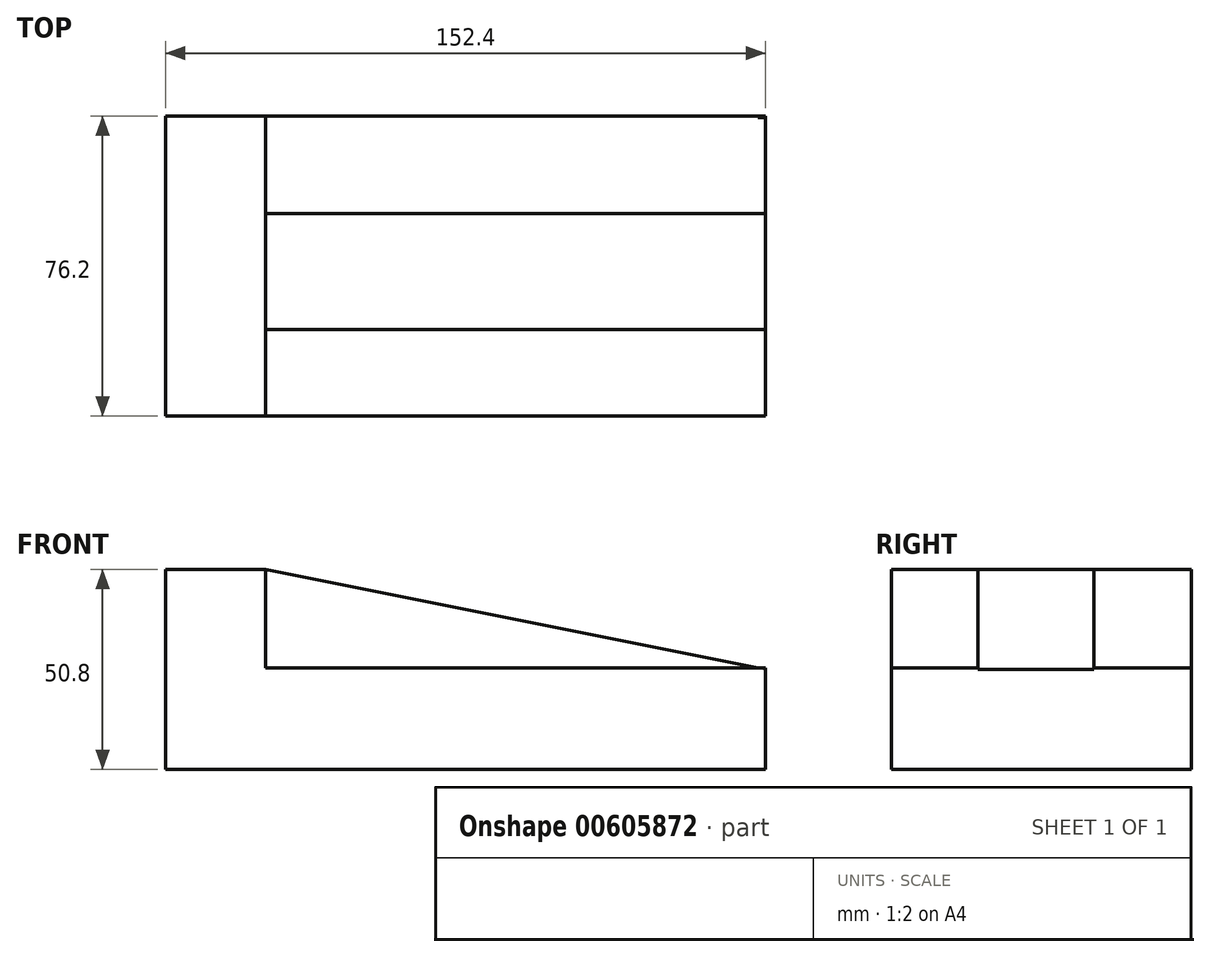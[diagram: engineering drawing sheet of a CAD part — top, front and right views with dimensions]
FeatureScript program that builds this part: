
annotation { "Feature Type Name" : "Feature", "Feature Type Description" : "" }
export const myFeature = defineFeature(function(context is Context, id is Id, definition is map)
    precondition{}
    {
        {
            var Q0;
            Q0=qCreatedBy(makeId("Front.planeOp"),FACE);
            var sketch = newSketch(context, id + "F0", { "sketchPlane" : qUnion([Q0])});
            skLineSegment(sketch, "E0", {"start": v(0, 0) * mm, "end": v(-152.4, 0) * mm});
            skLineSegment(sketch, "E1", {"start": v(-152.4, 0) * mm, "end": v(-152.4, 50.8) * mm});
            skLineSegment(sketch, "E2", {"start": v(-152.4, 50.8) * mm, "end": v(-127, 50.8) * mm});
            skLineSegment(sketch, "E3", {"start": v(-127, 50.8) * mm, "end": v(-127, 25.4) * mm});
            skLineSegment(sketch, "E4", {"start": v(0, 0) * mm, "end": v(0, 25.4) * mm});
            skLineSegment(sketch, "E5", {"start": v(-127, 25.4) * mm, "end": v(0, 25.4) * mm});
            skLineSegment(sketch, "E6", {"start": v(-127, 50.8) * mm, "end": v(0, 25.4) * mm});
            skSolve(sketch);
        }
        {
            var Q0;
            Q0=qCreatedBy(makeId("Right.planeOp"),FACE);
            var sketch = newSketch(context, id + "F1", { "sketchPlane" : qUnion([Q0])});
            skLineSegment(sketch, "E7", {"start": v(0, 0) * mm, "end": v(75.82, 0) * mm});
            skLineSegment(sketch, "E8", {"start": v(75.82, 0) * mm, "end": v(75.82, 51.18) * mm});
            skLineSegment(sketch, "E9", {"start": v(75.82, 51.18) * mm, "end": v(0, 51.18) * mm});
            skLineSegment(sketch, "E10", {"start": v(21.97, 51.18) * mm, "end": v(21.97, 0) * mm});
            skLineSegment(sketch, "E11", {"start": v(51.44, 51.18) * mm, "end": v(51.44, 0) * mm});
            skLineSegment(sketch, "E12", {"start": v(0, 51.18) * mm, "end": v(0, 0) * mm});
            skSolve(sketch);
        }
        {
            var Q0;
            Q0=makeQuery(id+"F0.imprint","IMPRINT",FACE,{"disambiguationData":[TD([[makeQuery(id+"F0.imprint","IMPRINT",EDGE,{"derivedFrom":sQuery(id+"F0.wireOp",EDGE,"E0")}),-1.0]])]});
            var Q1;
            Q1=makeQuery(id+"F0.imprint","IMPRINT",FACE,{"disambiguationData":[TD([[makeQuery(id+"F0.imprint","IMPRINT",EDGE,{"derivedFrom":sQuery(id+"F0.wireOp",EDGE,"E3")}),1.0]])]});
            extrude(context, id + "F2", {"entities" : qUnion([Q0, Q1]), "oppositeDirection" : true, "depth" : 76.2 * mm, "offsetDistance" : 25.4 * mm});
        }
        {
            var Q0;
            {var subQ2=sQuery(id+"F1.wireOp",EDGE,"E10");Q0=makeQuery(id+"F1.imprint","IMPRINT",FACE,{"disambiguationData":[TD([[makeQuery(id+"F1.imprint","IMPRINT",EDGE,{"derivedFrom":subQ2}),-1.0]])]});}
            extrude(context, id + "F3", {"entities" : qUnion([Q0]), "operationType" : NewBodyOperationType.ADD, "oppositeDirection" : true, "depth" : 127 * mm, "offsetDistance" : 25.4 * mm});
        }
        {
            var Q0;
            {var subQ0=sQuery(id+"F1.wireOp",EDGE,"E8");Q0=makeQuery(id+"F1.imprint","IMPRINT",FACE,{"disambiguationData":[TD([[makeQuery(id+"F1.imprint","IMPRINT",EDGE,{"derivedFrom":subQ0}),1.0]])]});}
            extrude(context, id + "F4", {"entities" : qUnion([Q0]), "operationType" : NewBodyOperationType.ADD, "oppositeDirection" : true, "depth" : 127 * mm, "offsetDistance" : 25.4 * mm});
        }
        {
            var Q0;
            Q0=makeQuery(id+"F3.opExtrude","SWEPT_FACE",FACE,{"disambiguationData":[OSD([sQuery(id+"F1.wireOp",EDGE,"E9")])]});
            var Q1;
            Q1=makeQuery(id+"F4.opExtrude","SWEPT_FACE",FACE,{"disambiguationData":[OSD([sQuery(id+"F1.wireOp",EDGE,"E9")])]});
            extrude(context, id + "F5", {"entities" : qUnion([Q0, Q1]), "operationType" : NewBodyOperationType.REMOVE, "oppositeDirection" : true, "depth" : 25.4 * mm, "offsetDistance" : 25.4 * mm});
        }
        {
            var Q0;
            Q0=makeQuery(id+"F5.boolean.opBoolean","COPY",FACE,{"derivedFrom":makeQuery(id+"F5.opExtrude","SWEPT_FACE",FACE,{"disambiguationData":[OSD([sQuery(id+"F1.wireOp",EDGE,"E8"),sQuery(id+"F1.wireOp",EDGE,"E9")])]})});
            extrude(context, id + "F6", {"entities" : qUnion([Q0]), "operationType" : NewBodyOperationType.REMOVE, "oppositeDirection" : true, "depth" : 25.4 * mm, "offsetDistance" : 25.4 * mm});
        }
    });
